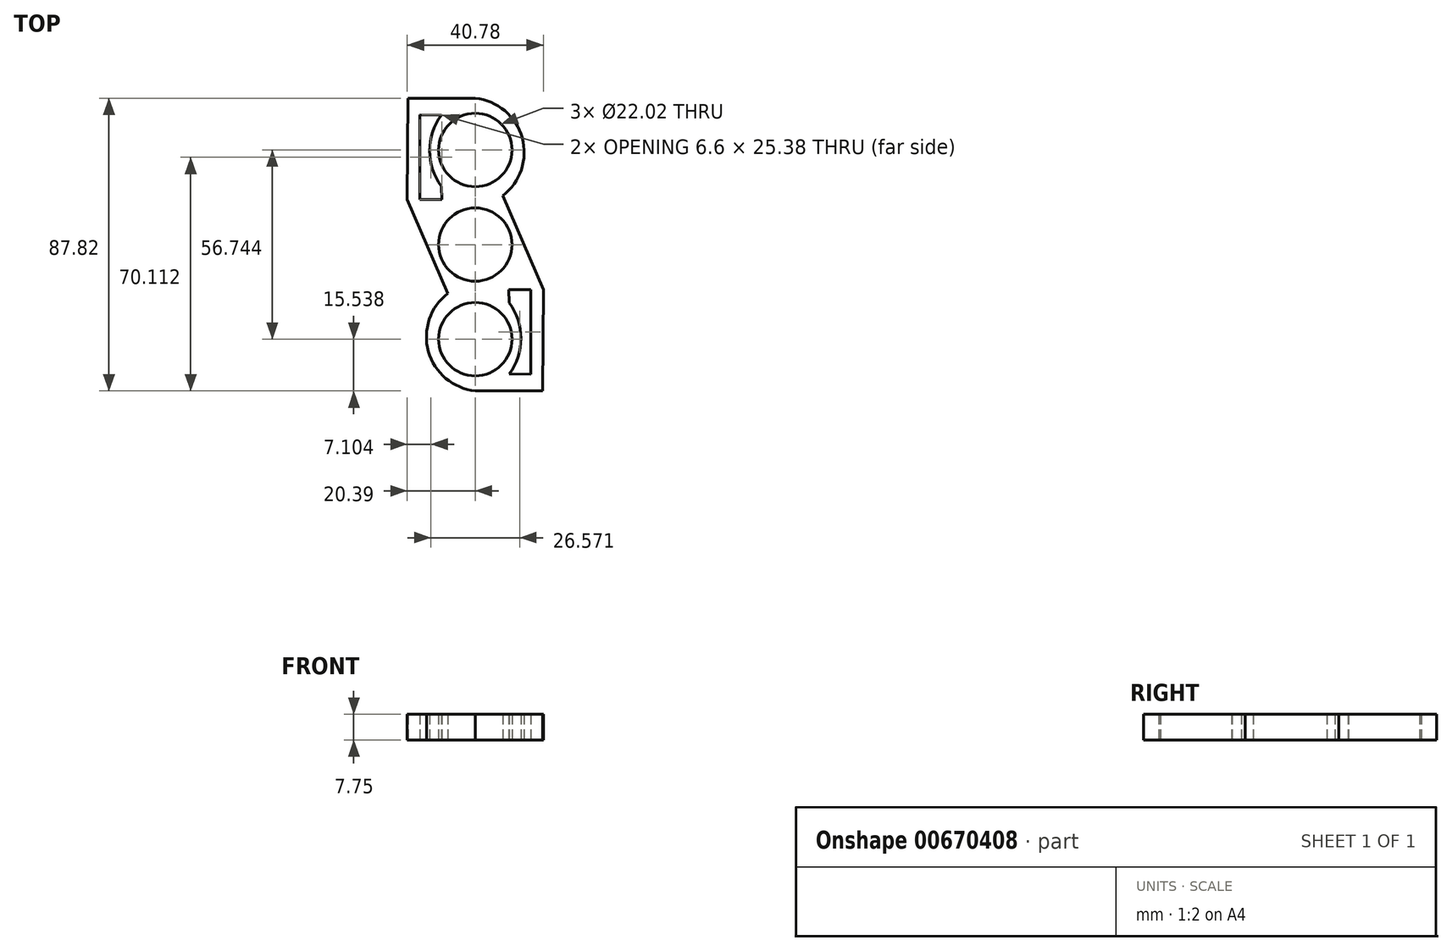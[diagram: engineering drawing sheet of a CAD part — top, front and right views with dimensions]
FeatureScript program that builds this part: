
annotation { "Feature Type Name" : "Feature", "Feature Type Description" : "" }
export const myFeature = defineFeature(function(context is Context, id is Id, definition is map)
    precondition{}
    {
        {
            var Q0;
            Q0=qCreatedBy(makeId("Top.planeOp"),FACE);
            var sketch = newSketch(context, id + "F0", { "sketchPlane" : qUnion([Q0])});
            skPoint(sketch, "E0.center.orphan", {"position": v(0, 26.45) * mm});
            skCircle(sketch, "E1", {"center": v(0, 0) * mm, "radius": 11.01 * mm});
            skCircle(sketch, "E2", {"center": v(0, 28.37) * mm, "radius": 11.01 * mm});
            skCircle(sketch, "E3", {"center": v(0, -28.37) * mm, "radius": 11.01 * mm});
            skPoint(sketch, "E4.endSnap0", {"position": v(-9.76, 9.2) * mm});
            skPoint(sketch, "E5.orphan", {"position": v(-13.24, 5.16) * mm});
            skPoint(sketch, "E6.orphan", {"position": v(-35.54, 56.17) * mm});
            skPoint(sketch, "E4.end.orphan", {"position": v(-9.76, 9.65) * mm});
            skPoint(sketch, "E7.end.orphan", {"position": v(-6.27, 13.24) * mm});
            skPoint(sketch, "E8.orphan", {"position": v(-6.83, 13.51) * mm});
            skPoint(sketch, "E9.top.end.orphan", {"position": v(-20.4, 13.51) * mm});
            skPoint(sketch, "E10.left.end.orphan", {"position": v(-22.86, 13.51) * mm});
            skPoint(sketch, "E10.top.end.orphan", {"position": v(-17.93, 13.51) * mm});
            skPoint(sketch, "E11.end.orphan", {"position": v(9.34, 56.17) * mm});
            skArc(sketch, "E12", {"start": v(8.22, 14.64) * mm, "mid": v(14.05, 32.06) * mm, "end": v(0, 43.9) * mm});
            skLineSegment(sketch, "E13", {"start": v(0, 43.9) * mm, "end": v(-20.21, 43.9) * mm});
            skLineSegment(sketch, "E14", {"start": v(-20.21, 43.9) * mm, "end": v(-20.4, 13.51) * mm});
            skPoint(sketch, "E15.orphan", {"position": v(-26.34, 43.9) * mm});
            skLineSegment(sketch, "E16", {"start": v(-16.59, 38.89) * mm, "end": v(-10.18, 38.85) * mm});
            skLineSegment(sketch, "E17", {"start": v(-16.59, 38.89) * mm, "end": v(-16.59, 13.51) * mm});
            skArc(sketch, "E18", {"start": v(-10.18, 38.85) * mm, "mid": v(-13.67, 28.16) * mm, "end": v(-10.18, 17.47) * mm});
            skLineSegment(sketch, "E19", {"start": v(-16.59, 13.51) * mm, "end": v(-9.98, 13.51) * mm});
            skLineSegment(sketch, "E20", {"start": v(-9.98, 13.51) * mm, "end": v(-10.18, 17.47) * mm});
            skLineSegment(sketch, "E21.1.0", {"start": v(0, -43.9) * mm, "end": v(20.21, -43.9) * mm});
            skArc(sketch, "E21.1.1", {"start": v(-8.22, -14.64) * mm, "mid": v(-14.05, -32.06) * mm, "end": v(0, -43.9) * mm});
            skLineSegment(sketch, "E21.1.2", {"start": v(20.21, -43.9) * mm, "end": v(20.4, -13.51) * mm});
            skLineSegment(sketch, "E21.1.3", {"start": v(16.59, -38.89) * mm, "end": v(16.59, -13.51) * mm});
            skLineSegment(sketch, "E21.1.4", {"start": v(16.59, -38.89) * mm, "end": v(10.18, -38.85) * mm});
            skArc(sketch, "E21.1.5", {"start": v(10.18, -38.85) * mm, "mid": v(13.67, -28.16) * mm, "end": v(10.18, -17.47) * mm});
            skLineSegment(sketch, "E21.1.6", {"start": v(16.59, -13.51) * mm, "end": v(9.98, -13.51) * mm});
            skLineSegment(sketch, "E21.1.7", {"start": v(9.98, -13.51) * mm, "end": v(10.18, -17.47) * mm});
            skLineSegment(sketch, "E22", {"start": v(8.22, 14.64) * mm, "end": v(20.4, -13.51) * mm});
            skLineSegment(sketch, "E23", {"start": v(-20.4, 13.51) * mm, "end": v(-8.22, -14.64) * mm});
            skSolve(sketch);
        }
        {
            var Q0;
            Q0 = qSketchRegion(id + "F0", true);
            extrude(context, id + "F1", {"entities" : qUnion([Q0]), "depth" : 7.75 * mm, "offsetDistance" : 25.4 * mm});
        }
    });
